# Revit family: P200921MX-073c_MZC31T15DW
name_source: partatom
category: Specialty Equipment
units: mm (PartAtom-declared; Revit-internal decimal feet)

## family parameters
Always vertical = Yes
Cut with Voids When Loaded = No
Enable Cutting in Views = No
Maintain Annotation Orientation = No
Part Type = Normal
Room Calculation Point = No
Round Connector Dimension = Use Diameter
Shared = No
Work Plane-Based = No

## types (1)
- MZC31T15DW
    Accent Material = ARCAT - Ruber -White
    Amps = 0 A
    Body Material = ARCAT - Metal - White
    Default Elevation = 0"
    Depth = 30 1/4"
    Description = 15 cu. ft. Chest Freezer with Door Lock
Congélateur horizontal Maytag® avec verrou de porte - 15 pi³
    Dimension Guide = http://access.whirlpool.com Guide&sku=MZC31T15DW&language=EN
http://access.whirlpool.com Guide&sku=MZC31T15DW&language=EN
    Door Material = ARCAT - Metal - White
    Energy Guide = http://access.whirlpool.com Guide&sku=MZC31T15DW&language=EN
http://access.whirlpool.com Guide&sku=MZC31T15DW&language=FR
ype=Energy Guide&sku=MZC3122FW&language=FR
    Family Name = Refrigeration
    Feature 1 = 10-Year Limited Parts Warranty on the Compressor
Garantie limitée de 10 ans sur les pièces du compresseur*
    Feature 2 = Incandescent Lighting
Éclairage incandescent
    Feature 3 = Freezer Door Lock
Type de porte du congélateur
    Height = 33 3/8"
    Manufacturer = Maytag
    Model = MZC31T15DW
    Voltage = 0 V
    Width = 47 3/8"

## geometry (parser evidence)
native form markers: Sweep x5
no freeform markers — native parametric forms only
